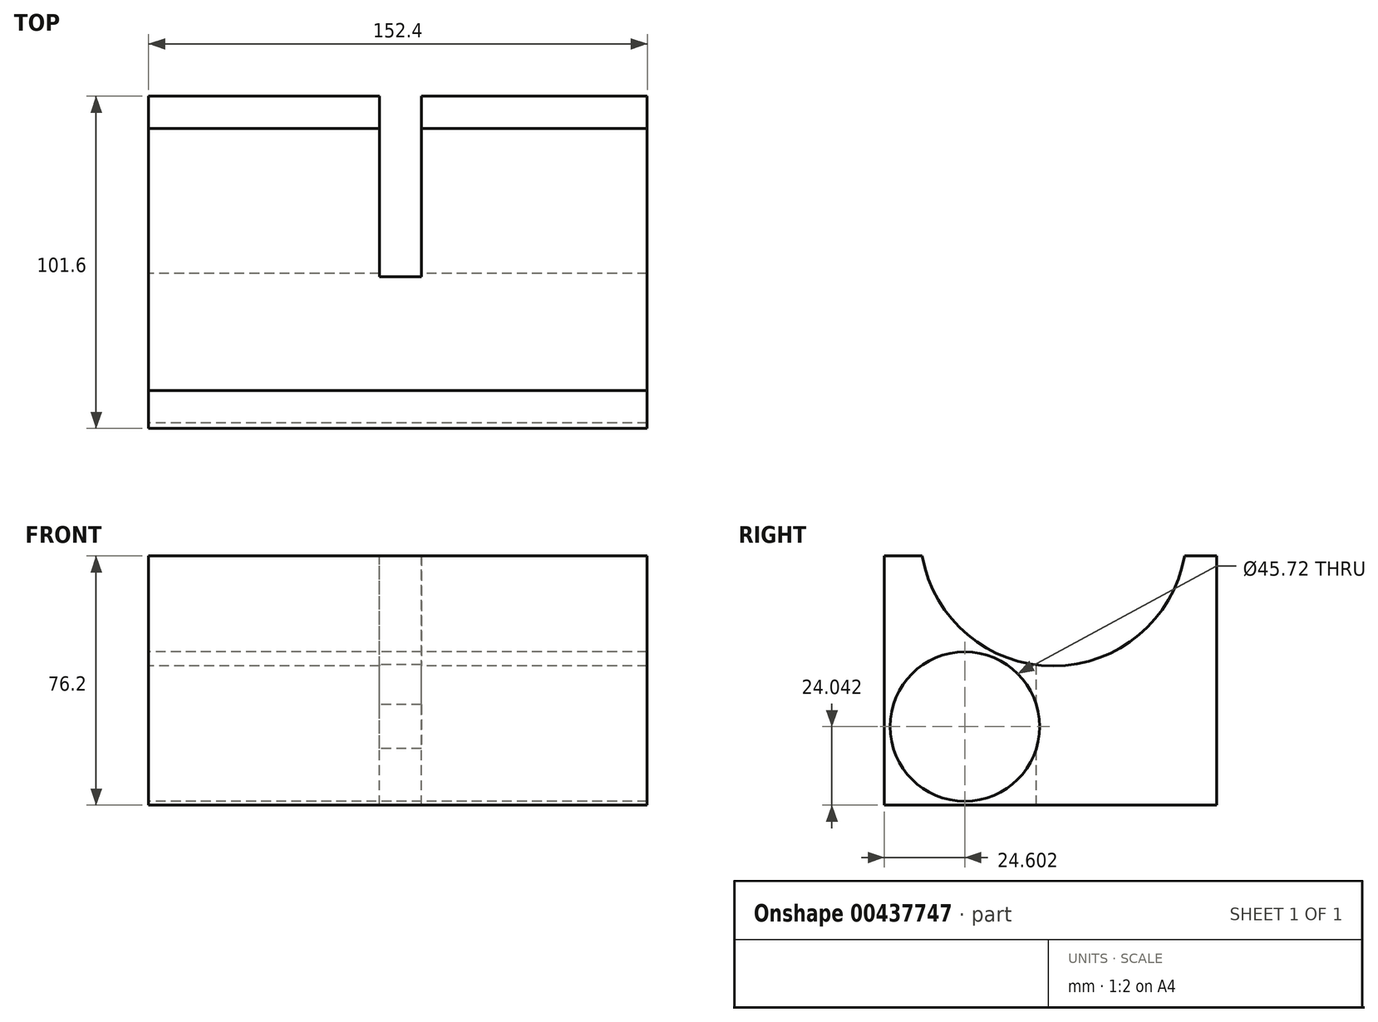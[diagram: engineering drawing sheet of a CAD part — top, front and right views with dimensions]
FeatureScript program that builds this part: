
annotation { "Feature Type Name" : "Feature", "Feature Type Description" : "" }
export const myFeature = defineFeature(function(context is Context, id is Id, definition is map)
    precondition{}
    {
        {
            var Q0;
            Q0=qCreatedBy(makeId("Top.planeOp"),FACE);
            var sketch = newSketch(context, id + "F0", { "sketchPlane" : qUnion([Q0])});
            skLineSegment(sketch, "E0", {"start": v(-41.6, 55.15) * mm, "end": v(-41.6, -46.45) * mm});
            skLineSegment(sketch, "E1", {"start": v(-41.6, -46.45) * mm, "end": v(110.8, -46.45) * mm});
            skLineSegment(sketch, "E2", {"start": v(110.8, -46.45) * mm, "end": v(110.8, 55.15) * mm});
            skLineSegment(sketch, "E3", {"start": v(110.8, 55.15) * mm, "end": v(-41.6, 55.15) * mm});
            skSolve(sketch);
        }
        {
            var Q0;
            Q0=makeQuery(id+"F0.imprint","IMPRINT",FACE,{"disambiguationData":[TD([[makeQuery(id+"F0.imprint","IMPRINT",EDGE,{"derivedFrom":sQuery(id+"F0.wireOp",EDGE,"E0")}),1.0]])]});
            extrude(context, id + "F1", {"entities" : qUnion([Q0]), "depth" : 76.2 * mm, "offsetDistance" : 25.4 * mm});
        }
        {
            var Q0;
            Q0=makeQuery(id+"F1.opExtrude","SWEPT_FACE",FACE,{"disambiguationData":[OSD([sQuery(id+"F0.wireOp",EDGE,"E0")])]});
            var sketch = newSketch(context, id + "F2", { "sketchPlane" : qUnion([Q0])});
            skArc(sketch, "E4", {"start": v(-45.31, 76.2) * mm, "mid": v(-5.21, 42.58) * mm, "end": v(34.89, 76.2) * mm});
            skSolve(sketch);
        }
        {
            var Q0;
            {var subQ0=sQuery(id+"F2.wireOp",EDGE,"E4");Q0=makeQuery(id+"F2.imprint","IMPRINT",FACE,{"disambiguationData":[TD([[makeQuery(id+"F2.imprint","IMPRINT",EDGE,{"derivedFrom":subQ0}),1.0]])]});}
            extrude(context, id + "F3", {"entities" : qUnion([Q0]), "operationType" : NewBodyOperationType.REMOVE, "oppositeDirection" : true, "depth" : 152.65 * mm, "offsetDistance" : 25.4 * mm});
        }
        {
            var Q0;
            {var subQ0=sQuery(id+"F0.wireOp",EDGE,"E0");var subQ1=sQuery(id+"F0.wireOp",EDGE,"E3");var subQ2=sQuery(id+"F0.wireOp",EDGE,"E2");Q0=makeQuery(id+"F3.boolean.opBoolean","SPLIT",FACE,{"disambiguationData":[TD([makeQuery(id+"F1.opExtrude","SWEPT_FACE",FACE,{"disambiguationData":[OSD([subQ1])]})])],"derivedFrom":makeQuery(id+"F1.opExtrude","CAP_FACE",FACE,{"disambiguationData":[OSD([subQ0,sQuery(id+"F0.wireOp",EDGE,"E1"),subQ2,subQ1])],"isStart":false})});}
            var sketch = newSketch(context, id + "F4", { "sketchPlane" : qUnion([Q0])});
            skLineSegment(sketch, "E5", {"start": v(41.71, 55.15) * mm, "end": v(41.71, 0) * mm});
            skLineSegment(sketch, "E6", {"start": v(29, 0) * mm, "end": v(41.71, 0) * mm});
            skLineSegment(sketch, "E7", {"start": v(29, 0) * mm, "end": v(29, 55.15) * mm});
            skLineSegment(sketch, "E8", {"start": v(41.71, 55.15) * mm, "end": v(29, 55.15) * mm});
            skSolve(sketch);
        }
        {
            var Q0;
            {var subQ0=sQuery(id+"F4.wireOp",EDGE,"E8");Q0=makeQuery(id+"F4.imprint","IMPRINT",FACE,{"disambiguationData":[TD([[makeQuery(id+"F4.imprint","IMPRINT",EDGE,{"derivedFrom":subQ0}),1.0]])]});}
            var Q1;
            {var subQ0=sQuery(id+"F4.wireOp",EDGE,"E6");Q1=makeQuery(id+"F4.imprint","IMPRINT",FACE,{"disambiguationData":[TD([[makeQuery(id+"F4.imprint","IMPRINT",EDGE,{"derivedFrom":subQ0}),1.0]])]});}
            extrude(context, id + "F5", {"entities" : qUnion([Q0, Q1]), "operationType" : NewBodyOperationType.REMOVE, "oppositeDirection" : true, "depth" : 115.32 * mm, "offsetDistance" : 25.4 * mm});
        }
        {
            var Q0;
            Q0=makeQuery(id+"F1.opExtrude","SWEPT_FACE",FACE,{"disambiguationData":[OSD([sQuery(id+"F0.wireOp",EDGE,"E0")])]});
            var sketch = newSketch(context, id + "F6", { "sketchPlane" : qUnion([Q0])});
            skCircle(sketch, "E9", {"center": v(21.85, 24.04) * mm, "radius": 22.86 * mm});
            skSolve(sketch);
        }
        {
            var Q0;
            Q0 = qSketchRegion(id + "F6", true);
            extrude(context, id + "F7", {"entities" : qUnion([Q0]), "operationType" : NewBodyOperationType.REMOVE, "oppositeDirection" : true, "depth" : 193.04 * mm, "offsetDistance" : 25.4 * mm});
        }
    });
